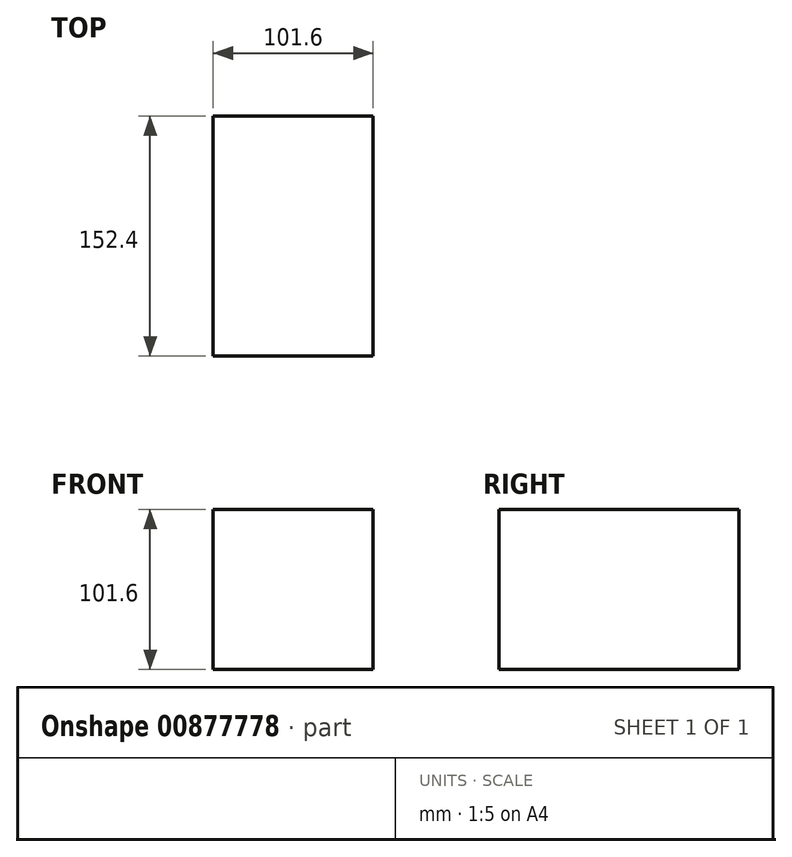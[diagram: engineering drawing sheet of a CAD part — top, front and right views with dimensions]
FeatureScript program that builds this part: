
annotation { "Feature Type Name" : "Feature", "Feature Type Description" : "" }
export const myFeature = defineFeature(function(context is Context, id is Id, definition is map)
    precondition{}
    {
        {
            var Q0;
            Q0=qCreatedBy(makeId("Top.planeOp"),FACE);
            var sketch = newSketch(context, id + "F0", { "sketchPlane" : qUnion([Q0])});
            skLineSegment(sketch, "E0.bottom", {"start": v(-82.6, 57.7) * mm, "end": v(19, 57.7) * mm});
            skLineSegment(sketch, "E0.top", {"start": v(-82.6, -94.7) * mm, "end": v(19, -94.7) * mm});
            skLineSegment(sketch, "E0.left", {"start": v(-82.6, 57.7) * mm, "end": v(-82.6, -94.7) * mm});
            skLineSegment(sketch, "E0.right", {"start": v(19, 57.7) * mm, "end": v(19, -94.7) * mm});
            skSolve(sketch);
        }
        {
            var Q0;
            Q0=makeQuery(id+"F0.imprint","IMPRINT",FACE,{"disambiguationData":[TD([[makeQuery(id+"F0.imprint","IMPRINT",EDGE,{"derivedFrom":sQuery(id+"F0.wireOp",EDGE,"E0.bottom")}),-1.0]])]});
            extrude(context, id + "F1", {"entities" : qUnion([Q0]), "depth" : 101.6 * mm, "offsetDistance" : 25.4 * mm});
        }
    });
